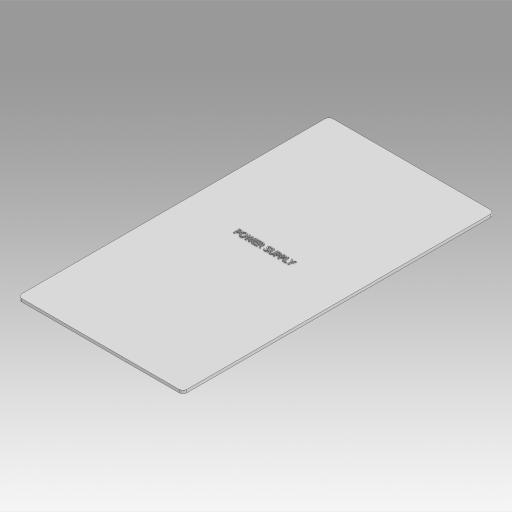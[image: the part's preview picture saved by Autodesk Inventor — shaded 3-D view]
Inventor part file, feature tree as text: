
AUTODESK INVENTOR PART (.ipt)
format: ipt  version: 2023 (Build 270158000, 158)  size: 444,416 bytes
history: native  units: mm
features: extrude x4, sketch x4, fillet x1, emboss x1, projected_geometry x1
ambient origin geometry x8: Origin, YZ Plane, XZ Plane, XY Plane, X Axis, Y Axis, Z Axis, Center Point
bodies: Solid1 (feature_tree)
feature tree (11):
  extrude  "Extrusion1"  Depth=160.0mm
  fillet  "Fillet1"  Radius=1.5mm
  sketch  "Sketch2"  dims[d4=2.0mm d5=2.5mm]
  extrude  "Extrusion2"  Depth=2.5mm
  extrude  "Extrusion3"  Depth=0.75mm TaperAngle=0.0deg
  extrude  "Extrusion4"  Depth=0.5mm
  emboss  "Emboss1"
  sketch  "Sketch1"  dims[d0=85.0mm d1=160.0mm d2=1.5mm d3=0.0mm]
  projected_geometry  "Projected Loop1"
  sketch  "Sketch3"  dims[d6=0.75mm d7=0.75mm d8=0.0mm]
  sketch  "Sketch4"  dims[d9=0.75mm d10=0.0mm d11=5.0mm d12=15.0mm d13=15.0mm d14=5.0mm d15=15.0mm d16=15.0mm d17=5.0mm d18=5.0mm d19=15.0mm d20=15.0mm d21=15.0mm d22=15.0mm d23=2.0mm d24=2.0mm d25=2.0mm d26=2.0mm d27=0.75mm d28=0.0mm d29=0.5mm d30=0.0mm]
